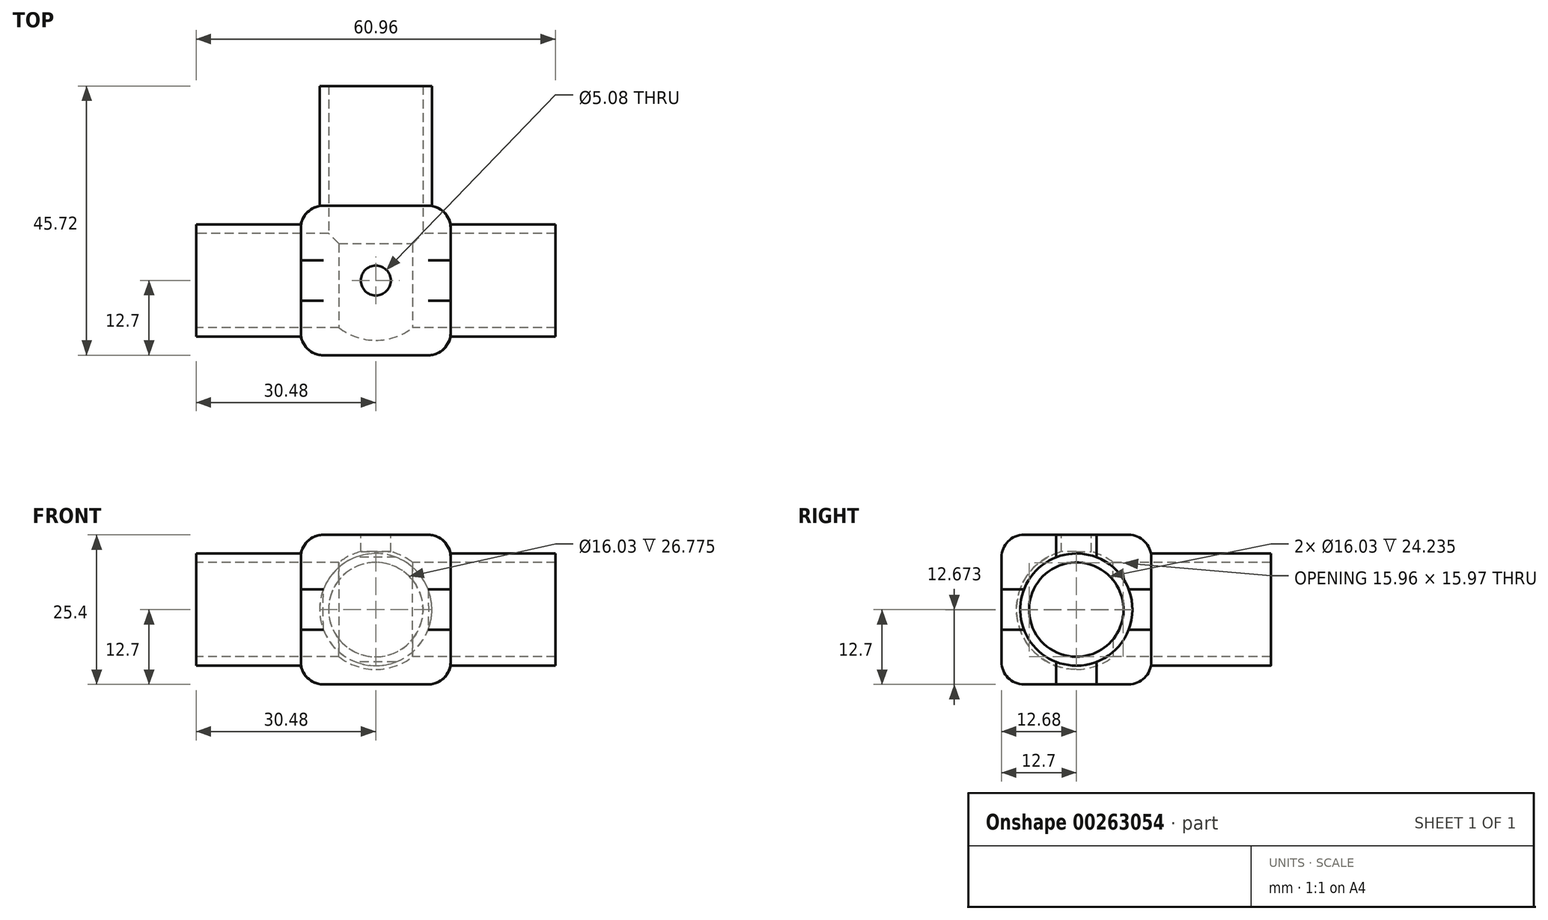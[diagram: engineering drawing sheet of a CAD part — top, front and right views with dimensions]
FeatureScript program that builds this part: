
annotation { "Feature Type Name" : "Feature", "Feature Type Description" : "" }
export const myFeature = defineFeature(function(context is Context, id is Id, definition is map)
    precondition{}
    {
        {
            var Q0;
            Q0=qCreatedBy(makeId("Right.planeOp"),FACE);
            var sketch = newSketch(context, id + "F0", { "sketchPlane" : qUnion([Q0])});
            skCircle(sketch, "E0", {"center": v(0, 0) * mm, "radius": 9.53 * mm});
            skCircle(sketch, "E1", {"center": v(0, 0) * mm, "radius": 8.01 * mm});
            skSolve(sketch);
        }
        {
            var Q0;
            Q0 = qSketchRegion(id + "F0", true);
            extrude(context, id + "F1", {"entities" : qUnion([Q0]), "endBound" : BoundingType.SYMMETRIC, "depth" : 60.96 * mm});
        }
        {
            var Q0;
            Q0=qCreatedBy(makeId("Top.planeOp"),FACE);
            var sketch = newSketch(context, id + "F2", { "sketchPlane" : qUnion([Q0])});
            skLineSegment(sketch, "E2.bottom", {"start": v(12.7, 12.7) * mm, "end": v(-12.7, 12.7) * mm});
            skLineSegment(sketch, "E2.top", {"start": v(12.7, -12.7) * mm, "end": v(-12.7, -12.7) * mm});
            skLineSegment(sketch, "E2.left", {"start": v(12.7, 12.7) * mm, "end": v(12.7, -12.7) * mm});
            skLineSegment(sketch, "E2.right", {"start": v(-12.7, 12.7) * mm, "end": v(-12.7, -12.7) * mm});
            skPoint(sketch, "E2.middle", {"position": v(0, 0) * mm});
            skSolve(sketch);
        }
        {
            var Q0;
            Q0 = qSketchRegion(id + "F2", true);
            extrude(context, id + "F3", {"entities" : qUnion([Q0]), "operationType" : NewBodyOperationType.ADD, "endBound" : BoundingType.SYMMETRIC, "depth" : 25.4 * mm});
        }
        {
            var Q0;
            Q0=makeQuery(id+"F3.boolean.opBoolean","SPLIT",FACE,{"disambiguationData":[TD([makeQuery(id+"F1.opExtrude","SWEPT_FACE",FACE,{"disambiguationData":[OSD([sQuery(id+"F0.wireOp",EDGE,"E1")])]})])],"derivedFrom":makeQuery(id+"F3.opExtrude","SWEPT_FACE",FACE,{"disambiguationData":[OSD([sQuery(id+"F2.wireOp",EDGE,"E2.right")])]})});
            var sketch = newSketch(context, id + "F4", { "sketchPlane" : qUnion([Q0])});
            skCircle(sketch, "E3", {"center": v(0, 0) * mm, "radius": 8.01 * mm});
            skSolve(sketch);
        }
        {
            var Q0;
            Q0 = qSketchRegion(id + "F4", true);
            var Q1;
            Q1=makeQuery(id+"F3.boolean.opBoolean","SPLIT",FACE,{"disambiguationData":[TD([makeQuery(id+"F1.opExtrude","SWEPT_FACE",FACE,{"disambiguationData":[OSD([sQuery(id+"F0.wireOp",EDGE,"E1")])]})])],"derivedFrom":makeQuery(id+"F3.opExtrude","SWEPT_FACE",FACE,{"disambiguationData":[OSD([sQuery(id+"F2.wireOp",EDGE,"E2.left")])]})});
            extrude(context, id + "F5", {"entities" : qUnion([Q0]), "operationType" : NewBodyOperationType.REMOVE, "endBound" : BoundingType.UP_TO_SURFACE, "oppositeDirection" : true, "endBoundEntityFace" : qUnion([Q1]), "depth" : 25.4 * mm});
        }
        {
            var Q0;
            Q0=qCreatedBy(makeId("Right.planeOp"),FACE);
            var sketch = newSketch(context, id + "F6", { "sketchPlane" : qUnion([Q0])});
            skLineSegment(sketch, "E4", {"start": v(0, 0) * mm, "end": v(0, 10.16) * mm});
            skLineSegment(sketch, "E5", {"start": v(0, 0) * mm, "end": v(0, -10.16) * mm});
            skArc(sketch, "E6", {"start": v(0, -10.16) * mm, "mid": v(10.16, 0) * mm, "end": v(0, 10.16) * mm});
            skSolve(sketch);
        }
        {
            var Q0;
            Q0=qCreatedBy(makeId("Top.planeOp"),FACE);
            var sketch = newSketch(context, id + "F7", { "sketchPlane" : qUnion([Q0])});
            skCircle(sketch, "E7", {"center": v(0, 0) * mm, "radius": 6.35 * mm});
            skSolve(sketch);
        }
        {
            var Q0;
            Q0=makeQuery(id+"F6.imprint","IMPRINT",FACE,{"disambiguationData":[TD([[makeQuery(id+"F6.imprint","IMPRINT",EDGE,{"derivedFrom":sQuery(id+"F6.wireOp",EDGE,"E4")}),-1.0]])]});
            var Q1;
            Q1=sQuery(id+"F7.wireOp",EDGE,"E7");
            revolve(context, id + "F8", {"operationType" : NewBodyOperationType.REMOVE, "entities" : qUnion([Q0]), "axis" : qUnion([Q1]), "revolveType" : RevolveType.FULL, "oppositeDirection" : true});
        }
        {
            var Q0;
            Q0=makeQuery(id+"F3.opExtrude","CAP_FACE",FACE,{"disambiguationData":[OSD([sQuery(id+"F2.wireOp",EDGE,"E2.bottom"),sQuery(id+"F2.wireOp",EDGE,"E2.top"),sQuery(id+"F2.wireOp",EDGE,"E2.left"),sQuery(id+"F2.wireOp",EDGE,"E2.right")])],"isStart":false});
            var sketch = newSketch(context, id + "F9", { "sketchPlane" : qUnion([Q0])});
            skCircle(sketch, "E8", {"center": v(0, 0) * mm, "radius": 2.54 * mm});
            skSolve(sketch);
        }
        {
            var Q0;
            Q0 = qSketchRegion(id + "F9", true);
            var Q1;
            Q1=makeQuery(id+"F8.boolean.opBoolean","COPY",FACE,{"derivedFrom":makeQuery(id+"F8.opRevolve","SWEPT_FACE",FACE,{"disambiguationData":[OSD([sQuery(id+"F6.wireOp",EDGE,"E6")])]})});
            extrude(context, id + "F10", {"entities" : qUnion([Q0]), "operationType" : NewBodyOperationType.REMOVE, "endBound" : BoundingType.UP_TO_SURFACE, "oppositeDirection" : true, "endBoundEntityFace" : qUnion([Q1]), "depth" : 25.4 * mm});
        }
        {
            var Q0;
            Q0=makeQuery(id+"F3.opExtrude","CAP_EDGE",EDGE,{"disambiguationData":[OSD([sQuery(id+"F2.wireOp",EDGE,"E2.left")])],"isStart":false});
            var Q1;
            Q1=makeQuery(id+"F3.opExtrude","CAP_EDGE",EDGE,{"disambiguationData":[OSD([sQuery(id+"F2.wireOp",EDGE,"E2.bottom")])],"isStart":false});
            var Q2;
            Q2=makeQuery(id+"F3.opExtrude","SWEPT_EDGE",EDGE,{"disambiguationData":[OSD([sQuery(id+"F2.wireOp",EDGE,"E2.bottom"),sQuery(id+"F2.wireOp",EDGE,"E2.left")])]});
            var Q3;
            Q3=makeQuery(id+"F3.opExtrude","SWEPT_EDGE",EDGE,{"disambiguationData":[OSD([sQuery(id+"F2.wireOp",EDGE,"E2.bottom"),sQuery(id+"F2.wireOp",EDGE,"E2.right")])]});
            var Q4;
            Q4=makeQuery(id+"F3.opExtrude","CAP_EDGE",EDGE,{"disambiguationData":[OSD([sQuery(id+"F2.wireOp",EDGE,"E2.right")])],"isStart":false});
            var Q5;
            Q5=makeQuery(id+"F3.opExtrude","CAP_EDGE",EDGE,{"disambiguationData":[OSD([sQuery(id+"F2.wireOp",EDGE,"E2.top")])],"isStart":false});
            var Q6;
            Q6=makeQuery(id+"F3.opExtrude","SWEPT_EDGE",EDGE,{"disambiguationData":[OSD([sQuery(id+"F2.wireOp",EDGE,"E2.top"),sQuery(id+"F2.wireOp",EDGE,"E2.left")])]});
            var Q7;
            Q7=makeQuery(id+"F3.opExtrude","SWEPT_EDGE",EDGE,{"disambiguationData":[OSD([sQuery(id+"F2.wireOp",EDGE,"E2.top"),sQuery(id+"F2.wireOp",EDGE,"E2.right")])]});
            var Q8;
            Q8=makeQuery(id+"F3.opExtrude","CAP_EDGE",EDGE,{"disambiguationData":[OSD([sQuery(id+"F2.wireOp",EDGE,"E2.top")])],"isStart":true});
            var Q9;
            Q9=makeQuery(id+"F3.opExtrude","CAP_EDGE",EDGE,{"disambiguationData":[OSD([sQuery(id+"F2.wireOp",EDGE,"E2.left")])],"isStart":true});
            var Q10;
            Q10=makeQuery(id+"F3.opExtrude","CAP_EDGE",EDGE,{"disambiguationData":[OSD([sQuery(id+"F2.wireOp",EDGE,"E2.right")])],"isStart":true});
            var Q11;
            Q11=makeQuery(id+"F3.opExtrude","CAP_EDGE",EDGE,{"disambiguationData":[OSD([sQuery(id+"F2.wireOp",EDGE,"E2.bottom")])],"isStart":true});
            fillet(context, id + "F11", {"entities" : qUnion([Q0, Q1, Q2, Q3, Q4, Q5, Q6, Q7, Q8, Q9, Q10, Q11]), "radius" : 3.8 * mm, "tangentPropagation" : true, "allowEdgeOverflow" : false});
        }
        {
            var Q0;
            Q0=makeQuery(id+"F3.opExtrude","SWEPT_FACE",FACE,{"disambiguationData":[OSD([sQuery(id+"F2.wireOp",EDGE,"E2.bottom")])]});
            var sketch = newSketch(context, id + "F12", { "sketchPlane" : qUnion([Q0])});
            skCircle(sketch, "E9", {"center": v(0, 0) * mm, "radius": 9.53 * mm});
            skCircle(sketch, "E10", {"center": v(0, 0) * mm, "radius": 8.01 * mm});
            skSolve(sketch);
        }
        {
            var Q0;
            Q0 = qSketchRegion(id + "F12", true);
            extrude(context, id + "F13", {"entities" : qUnion([Q0]), "operationType" : NewBodyOperationType.ADD, "depth" : 20.32 * mm});
        }
        {
            var Q0;
            Q0=makeQuery(id+"F13.boolean.opBoolean","SPLIT",FACE,{"disambiguationData":[TD([makeQuery(id+"F13.opExtrude","SWEPT_FACE",FACE,{"disambiguationData":[OSD([sQuery(id+"F12.wireOp",EDGE,"E10")])]})])],"derivedFrom":makeQuery(id+"F3.opExtrude","SWEPT_FACE",FACE,{"disambiguationData":[OSD([sQuery(id+"F2.wireOp",EDGE,"E2.bottom")])]})});
            var sketch = newSketch(context, id + "F14", { "sketchPlane" : qUnion([Q0])});
            skCircle(sketch, "E11", {"center": v(0, 0) * mm, "radius": 8.01 * mm});
            skSolve(sketch);
        }
        {
            var Q0;
            Q0 = qSketchRegion(id + "F14", true);
            var Q1;
            Q1=makeQuery(id+"F8.boolean.opBoolean","COPY",FACE,{"derivedFrom":makeQuery(id+"F8.opRevolve","SWEPT_FACE",FACE,{"disambiguationData":[OSD([sQuery(id+"F6.wireOp",EDGE,"E6")])]})});
            extrude(context, id + "F15", {"entities" : qUnion([Q0]), "operationType" : NewBodyOperationType.REMOVE, "endBound" : BoundingType.UP_TO_SURFACE, "oppositeDirection" : true, "endBoundEntityFace" : qUnion([Q1]), "depth" : 25.4 * mm});
        }
    });
